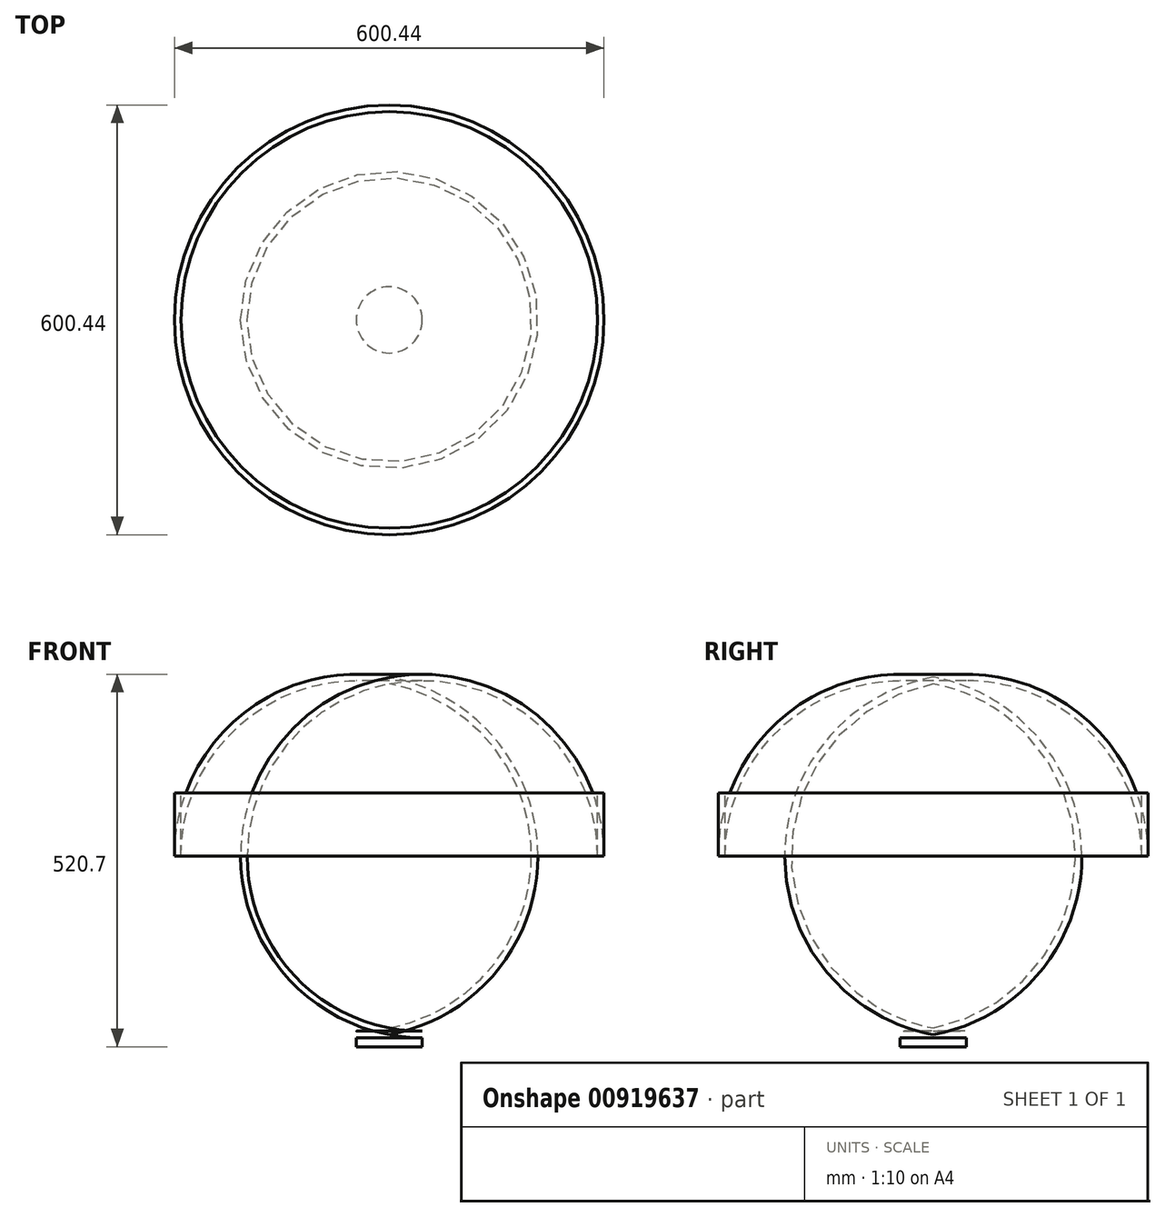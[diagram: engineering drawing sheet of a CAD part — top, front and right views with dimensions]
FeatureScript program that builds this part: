
annotation { "Feature Type Name" : "Feature", "Feature Type Description" : "" }
export const myFeature = defineFeature(function(context is Context, id is Id, definition is map)
    precondition{}
    {
        {
            var Q0;
            Q0=qCreatedBy(makeId("Front.planeOp"),FACE);
            var sketch = newSketch(context, id + "F0", { "sketchPlane" : qUnion([Q0])});
            skLineSegment(sketch, "E0", {"start": v(0, 0) * mm, "end": v(46.22, 0) * mm});
            skLineSegment(sketch, "E1", {"start": v(46.22, 0) * mm, "end": v(46.22, 0) * mm});
            skLineSegment(sketch, "E2", {"start": v(300.22, 254) * mm, "end": v(300.22, 342.28) * mm});
            skPoint(sketch, "E3.visualSharp", {"position": v(300.22, 0) * mm});
            skArc(sketch, "E3.filletArc", {"start": v(46.22, 0) * mm, "mid": v(225.82, 74.4) * mm, "end": v(300.22, 254) * mm});
            skLineSegment(sketch, "E4.0", {"start": v(291.15, 254) * mm, "end": v(291.15, 342.28) * mm});
            skArc(sketch, "E4.1", {"start": v(46.22, 9.07) * mm, "mid": v(219.41, 80.8) * mm, "end": v(291.15, 254) * mm});
            skLineSegment(sketch, "E5", {"start": v(291.15, 342.28) * mm, "end": v(300.22, 342.28) * mm});
            skLineSegment(sketch, "E6", {"start": v(46.22, 9.07) * mm, "end": v(0, 9.07) * mm});
            skLineSegment(sketch, "E7", {"start": v(0, 9.07) * mm, "end": v(0, 0) * mm});
            skSolve(sketch);
        }
        {
            var Q0;
            Q0=makeQuery(id+"F0.imprint","IMPRINT",FACE,{"disambiguationData":[TD([[makeQuery(id+"F0.imprint","IMPRINT",EDGE,{"derivedFrom":sQuery(id+"F0.wireOp",EDGE,"E0")}),1.0]])]});
            var Q1;
            Q1=sQuery(id+"F0.wireOp",EDGE,"E7");
            revolve(context, id + "F1", {"surfaceOperationType" : NewSurfaceOperationType.NEW, "entities" : qUnion([Q0]), "axis" : qUnion([Q1]), "revolveType" : RevolveType.FULL});
        }
        {
            var Q0;
            Q0=makeQuery(id+"F1.opRevolve","SWEPT_FACE",FACE,{"disambiguationData":[OSD([sQuery(id+"F0.wireOp",EDGE,"E0")])]});
            var sketch = newSketch(context, id + "F2", { "sketchPlane" : qUnion([Q0])});
            skCircle(sketch, "E8.0.0", {"center": v(0, 0) * mm, "radius": 46.22 * mm});
            skSolve(sketch);
        }
        {
            var Q0;
            Q0=makeQuery(id+"F2.imprint","IMPRINT",FACE,{"disambiguationData":[TD([[makeQuery(id+"F2.imprint","IMPRINT",EDGE,{"derivedFrom":sQuery(id+"F2.wireOp",EDGE,"E8.0.0")}),-1.0]])]});
            extrude(context, id + "F3", {"entities" : qUnion([Q0]), "operationType" : NewBodyOperationType.ADD, "depth" : 12.7 * mm, "offsetDistance" : 25.4 * mm});
        }
    });
